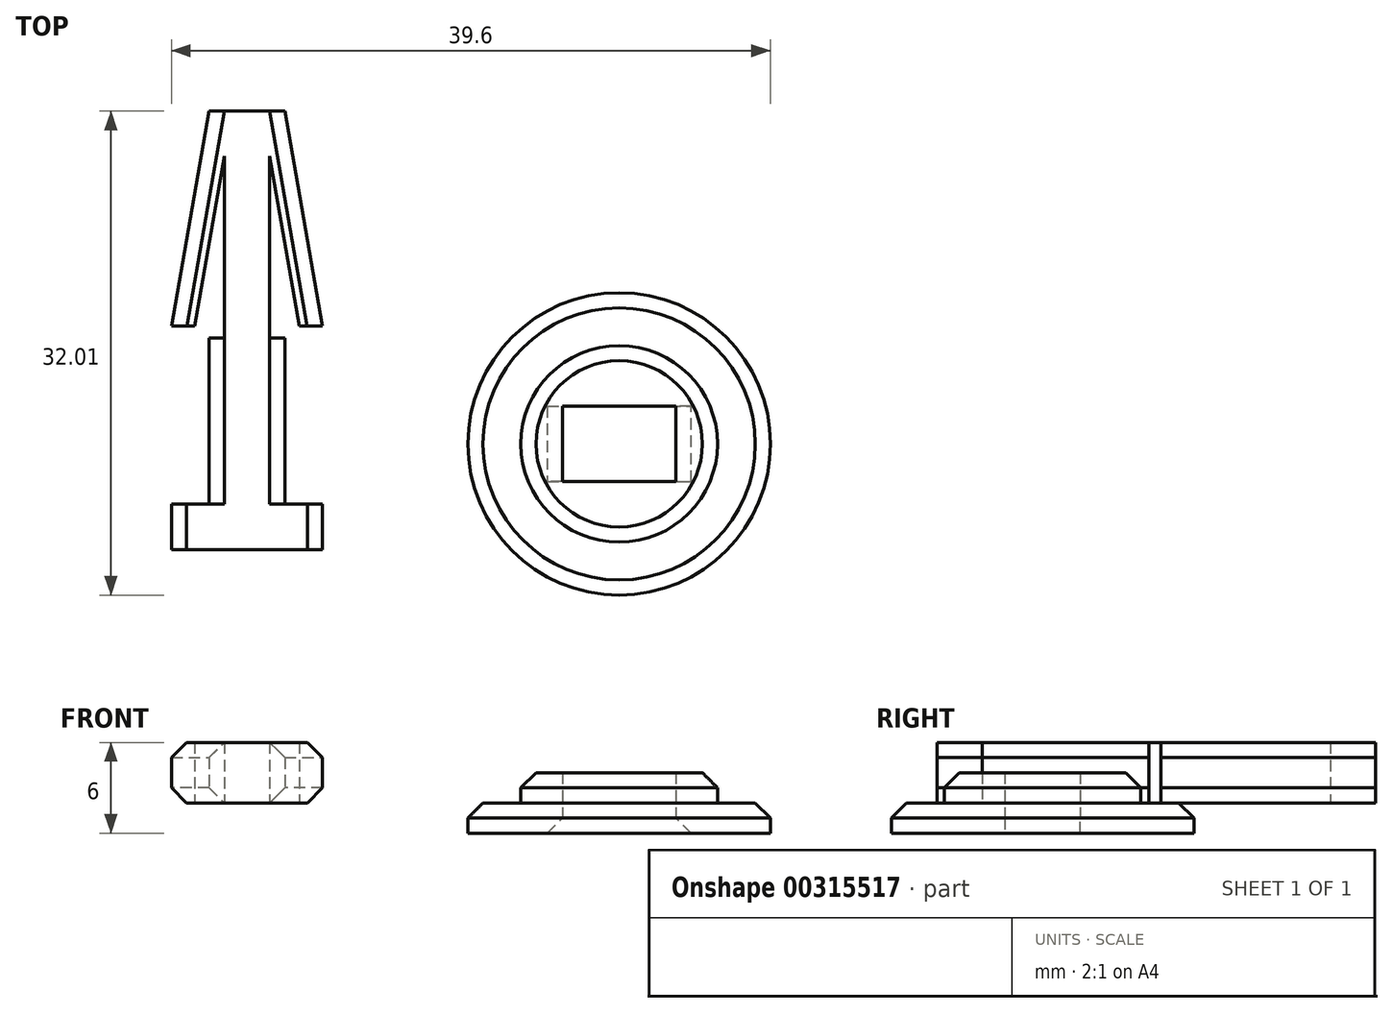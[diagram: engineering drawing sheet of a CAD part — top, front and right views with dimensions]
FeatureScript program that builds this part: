
annotation { "Feature Type Name" : "Feature", "Feature Type Description" : "" }
export const myFeature = defineFeature(function(context is Context, id is Id, definition is map)
    precondition{}
    {
        {
            var Q0;
            Q0=qCreatedBy(makeId("Top.planeOp"),FACE);
            var sketch = newSketch(context, id + "F0", { "sketchPlane" : qUnion([Q0])});
            skLineSegment(sketch, "E0", {"start": v(-5, 14.8) * mm, "end": v(-3.48, 14.8) * mm});
            skLineSegment(sketch, "E1", {"start": v(-3.48, 14.8) * mm, "end": v(-1.5, 26.03) * mm});
            skLineSegment(sketch, "E2", {"start": v(-1.5, 26.03) * mm, "end": v(-1.5, 14) * mm});
            skLineSegment(sketch, "E3", {"start": v(-1.5, 14) * mm, "end": v(-2.5, 14) * mm});
            skLineSegment(sketch, "E4", {"start": v(-2.5, 14) * mm, "end": v(-2.5, 3) * mm});
            skLineSegment(sketch, "E5", {"start": v(-2.5, 3) * mm, "end": v(-5, 3) * mm});
            skLineSegment(sketch, "E6", {"start": v(-5, 3) * mm, "end": v(-5, 0) * mm});
            skLineSegment(sketch, "E7", {"start": v(-5, 0) * mm, "end": v(5, 0) * mm});
            skLineSegment(sketch, "E8", {"start": v(5, 0) * mm, "end": v(5, 3) * mm});
            skLineSegment(sketch, "E9", {"start": v(5, 3) * mm, "end": v(2.5, 3) * mm});
            skLineSegment(sketch, "E10", {"start": v(2.5, 3) * mm, "end": v(2.5, 14) * mm});
            skLineSegment(sketch, "E11", {"start": v(2.5, 14) * mm, "end": v(1.5, 14) * mm});
            skLineSegment(sketch, "E12", {"start": v(1.5, 14) * mm, "end": v(1.5, 26.03) * mm});
            skLineSegment(sketch, "E13", {"start": v(1.5, 26.03) * mm, "end": v(3.48, 14.8) * mm});
            skLineSegment(sketch, "E14", {"start": v(3.48, 14.8) * mm, "end": v(5, 14.8) * mm});
            skLineSegment(sketch, "E15", {"start": v(5, 14.8) * mm, "end": v(2.5, 29) * mm});
            skLineSegment(sketch, "E16", {"start": v(2.5, 29) * mm, "end": v(-2.5, 29) * mm});
            skLineSegment(sketch, "E17", {"start": v(-2.5, 29) * mm, "end": v(-5, 14.8) * mm});
            skPoint(sketch, "E18", {"position": v(0, 0) * mm});
            skPoint(sketch, "E19", {"position": v(0, 29) * mm});
            skLineSegment(sketch, "E20", {"start": v(-1.5, 14) * mm, "end": v(1.5, 14) * mm, "construction": true});
            skLineSegment(sketch, "E21", {"start": v(-2.5, 3) * mm, "end": v(2.5, 3) * mm, "construction": true});
            skPoint(sketch, "E22", {"position": v(0, 3) * mm});
            skPoint(sketch, "E23", {"position": v(0, 14) * mm});
            skSolve(sketch);
        }
        {
            var Q0;
            Q0 = qSketchRegion(id + "F0", true);
            extrude(context, id + "F1", {"entities" : qUnion([Q0]), "depth" : 4 * mm});
        }
        {
            var Q0;
            Q0=qCreatedBy(makeId("Top.planeOp"),FACE);
            var sketch = newSketch(context, id + "F2", { "sketchPlane" : qUnion([Q0])});
            skCircle(sketch, "E24", {"center": v(24.6, 7) * mm, "radius": 6.5 * mm});
            skLineSegment(sketch, "E25.bottom", {"start": v(20.85, 9.5) * mm, "end": v(28.35, 9.5) * mm});
            skLineSegment(sketch, "E25.top", {"start": v(20.85, 4.5) * mm, "end": v(28.35, 4.5) * mm});
            skLineSegment(sketch, "E25.left", {"start": v(20.85, 9.5) * mm, "end": v(20.85, 4.5) * mm});
            skLineSegment(sketch, "E25.right", {"start": v(28.35, 9.5) * mm, "end": v(28.35, 4.5) * mm});
            skPoint(sketch, "E26", {"position": v(20.85, 7) * mm});
            skPoint(sketch, "E27", {"position": v(24.6, 9.5) * mm});
            skSolve(sketch);
        }
        {
            var Q0;
            Q0=makeQuery(id+"F2.imprint","IMPRINT",FACE,{"disambiguationData":[TD([[makeQuery(id+"F2.imprint","IMPRINT",EDGE,{"derivedFrom":sQuery(id+"F2.wireOp",EDGE,"E24")}),1.0]])]});
            extrude(context, id + "F3", {"entities" : qUnion([Q0]), "depth" : 2 * mm});
        }
        {
            var Q0;
            Q0=makeQuery(id+"F1.opExtrude","CAP_EDGE",EDGE,{"disambiguationData":[OSD([sQuery(id+"F0.wireOp",EDGE,"E10")])],"isStart":true});
            var Q1;
            Q1=makeQuery(id+"F1.opExtrude","CAP_EDGE",EDGE,{"disambiguationData":[OSD([sQuery(id+"F0.wireOp",EDGE,"E15")])],"isStart":true});
            var Q2;
            Q2=makeQuery(id+"F1.opExtrude","CAP_EDGE",EDGE,{"disambiguationData":[OSD([sQuery(id+"F0.wireOp",EDGE,"E4")])],"isStart":true});
            var Q3;
            Q3=makeQuery(id+"F1.opExtrude","CAP_EDGE",EDGE,{"disambiguationData":[OSD([sQuery(id+"F0.wireOp",EDGE,"E17")])],"isStart":true});
            var Q4;
            Q4=makeQuery(id+"F1.opExtrude","CAP_EDGE",EDGE,{"disambiguationData":[OSD([sQuery(id+"F0.wireOp",EDGE,"E4")])],"isStart":false});
            var Q5;
            Q5=makeQuery(id+"F1.opExtrude","CAP_EDGE",EDGE,{"disambiguationData":[OSD([sQuery(id+"F0.wireOp",EDGE,"E10")])],"isStart":false});
            var Q6;
            Q6=makeQuery(id+"F1.opExtrude","CAP_EDGE",EDGE,{"disambiguationData":[OSD([sQuery(id+"F0.wireOp",EDGE,"E15")])],"isStart":false});
            var Q7;
            Q7=makeQuery(id+"F1.opExtrude","CAP_EDGE",EDGE,{"disambiguationData":[OSD([sQuery(id+"F0.wireOp",EDGE,"E17")])],"isStart":false});
            chamfer(context, id + "F4", {"entities" : qUnion([Q0, Q1, Q2, Q3, Q4, Q5, Q6, Q7]), "width" : 1 * mm, "tangentPropagation" : true});
        }
        {
            var Q0;
            Q0=makeQuery(id+"F1.opExtrude","CAP_EDGE",EDGE,{"disambiguationData":[OSD([sQuery(id+"F0.wireOp",EDGE,"E8")])],"isStart":true});
            var Q1;
            Q1=makeQuery(id+"F1.opExtrude","CAP_EDGE",EDGE,{"disambiguationData":[OSD([sQuery(id+"F0.wireOp",EDGE,"E6")])],"isStart":true});
            var Q2;
            Q2=makeQuery(id+"F1.opExtrude","CAP_EDGE",EDGE,{"disambiguationData":[OSD([sQuery(id+"F0.wireOp",EDGE,"E6")])],"isStart":false});
            var Q3;
            Q3=makeQuery(id+"F1.opExtrude","CAP_EDGE",EDGE,{"disambiguationData":[OSD([sQuery(id+"F0.wireOp",EDGE,"E8")])],"isStart":false});
            chamfer(context, id + "F5", {"entities" : qUnion([Q0, Q1, Q2, Q3]), "width" : 1 * mm, "tangentPropagation" : true});
        }
        {
            var Q0;
            Q0=makeQuery(id+"F3.opExtrude","CAP_FACE",FACE,{"disambiguationData":[OSD([sQuery(id+"F2.wireOp",EDGE,"E24"),sQuery(id+"F2.wireOp",EDGE,"E25.bottom"),sQuery(id+"F2.wireOp",EDGE,"E25.top"),sQuery(id+"F2.wireOp",EDGE,"E25.left"),sQuery(id+"F2.wireOp",EDGE,"E25.right")])],"isStart":true});
            var sketch = newSketch(context, id + "F6", { "sketchPlane" : qUnion([Q0])});
            skCircle(sketch, "E28", {"center": v(24.6, -7) * mm, "radius": 10 * mm});
            skLineSegment(sketch, "E29.bottom", {"start": v(20.85, -4.5) * mm, "end": v(28.35, -4.5) * mm});
            skLineSegment(sketch, "E29.top", {"start": v(20.85, -9.5) * mm, "end": v(28.35, -9.5) * mm});
            skLineSegment(sketch, "E29.left", {"start": v(20.85, -4.5) * mm, "end": v(20.85, -9.5) * mm});
            skLineSegment(sketch, "E29.right", {"start": v(28.35, -4.5) * mm, "end": v(28.35, -9.5) * mm});
            skSolve(sketch);
        }
        {
            var Q0;
            Q0 = qSketchRegion(id + "F6", true);
            extrude(context, id + "F7", {"entities" : qUnion([Q0]), "operationType" : NewBodyOperationType.ADD, "depth" : 2 * mm});
        }
        {
            var Q0;
            Q0=makeQuery(id+"F7.opExtrude","CAP_EDGE",EDGE,{"disambiguationData":[OSD([sQuery(id+"F6.wireOp",EDGE,"E29.left")])],"isStart":false});
            var Q1;
            Q1=makeQuery(id+"F7.opExtrude","CAP_EDGE",EDGE,{"disambiguationData":[OSD([sQuery(id+"F6.wireOp",EDGE,"E29.right")])],"isStart":false});
            var Q2;
            Q2=makeQuery(id+"F3.opExtrude","CAP_EDGE",EDGE,{"disambiguationData":[OSD([sQuery(id+"F2.wireOp",EDGE,"E24")])],"isStart":false});
            var Q3;
            Q3=makeQuery(id+"F7.opExtrude","CAP_EDGE",EDGE,{"disambiguationData":[OSD([sQuery(id+"F6.wireOp",EDGE,"E28")])],"isStart":true});
            chamfer(context, id + "F8", {"entities" : qUnion([Q0, Q1, Q2, Q3]), "width" : 1 * mm, "tangentPropagation" : true});
        }
    });
